# Revit family: Vanity_-_Protruding_Bowl_2760
name_source: partatom
category: Casework
units: mm (PartAtom-declared; Revit-internal decimal feet)

## family parameters
Always vertical = Yes
Cut with Voids When Loaded = No
Room Calculation Point = No
Shared = No
Work Plane-Based = No

## types (5) — shared parameters
Depth = 315 mm  [stored 1.03346 ft]
Description = "Cabinet - Vanity"
Height = 680 mm  [stored 2.23097 ft]
Kick Back Height = 150 mm
Kick Back Width = 65 mm  [stored 0.213255 ft]
zero-valued in all types: Default Elevation

## per-type parameters (varying)
| type | 1/2 Width | Centre | Door Right | Left Side | Right Side | Width |
| 900 | 470 mm  [stored 1.54199 ft] | 470 mm  [stored 1.54199 ft] | 470 mm  [stored 1.54199 ft] | 187 mm | 187 mm | 940 mm  [stored 3.08399 ft] |
| 750 | 375 mm  [stored 1.23031 ft] | 375 mm  [stored 1.23031 ft] | 375 mm  [stored 1.23031 ft] | 92 mm | 92 mm | 750 mm  [stored 2.46063 ft] |
| 600 | 300 mm | 300 mm | 300 mm | 17 mm | 17 mm | 600 mm |
| 1000 | 500 mm  [stored 1.64042 ft] | 500 mm  [stored 1.64042 ft] | 500 mm  [stored 1.64042 ft] | 217 mm | 217 mm | 1000 mm  [stored 3.28084 ft] |
| 1200 | 600 mm | 600 mm | 600 mm | 317 mm | 317 mm | 1200 mm |

note: [stored X ft] marks values corroborated as IEEE doubles in the binary element streams (Revit-internal decimal feet)

## geometry (parser evidence)
native form markers: Sweep x10
no freeform markers — native parametric forms only
